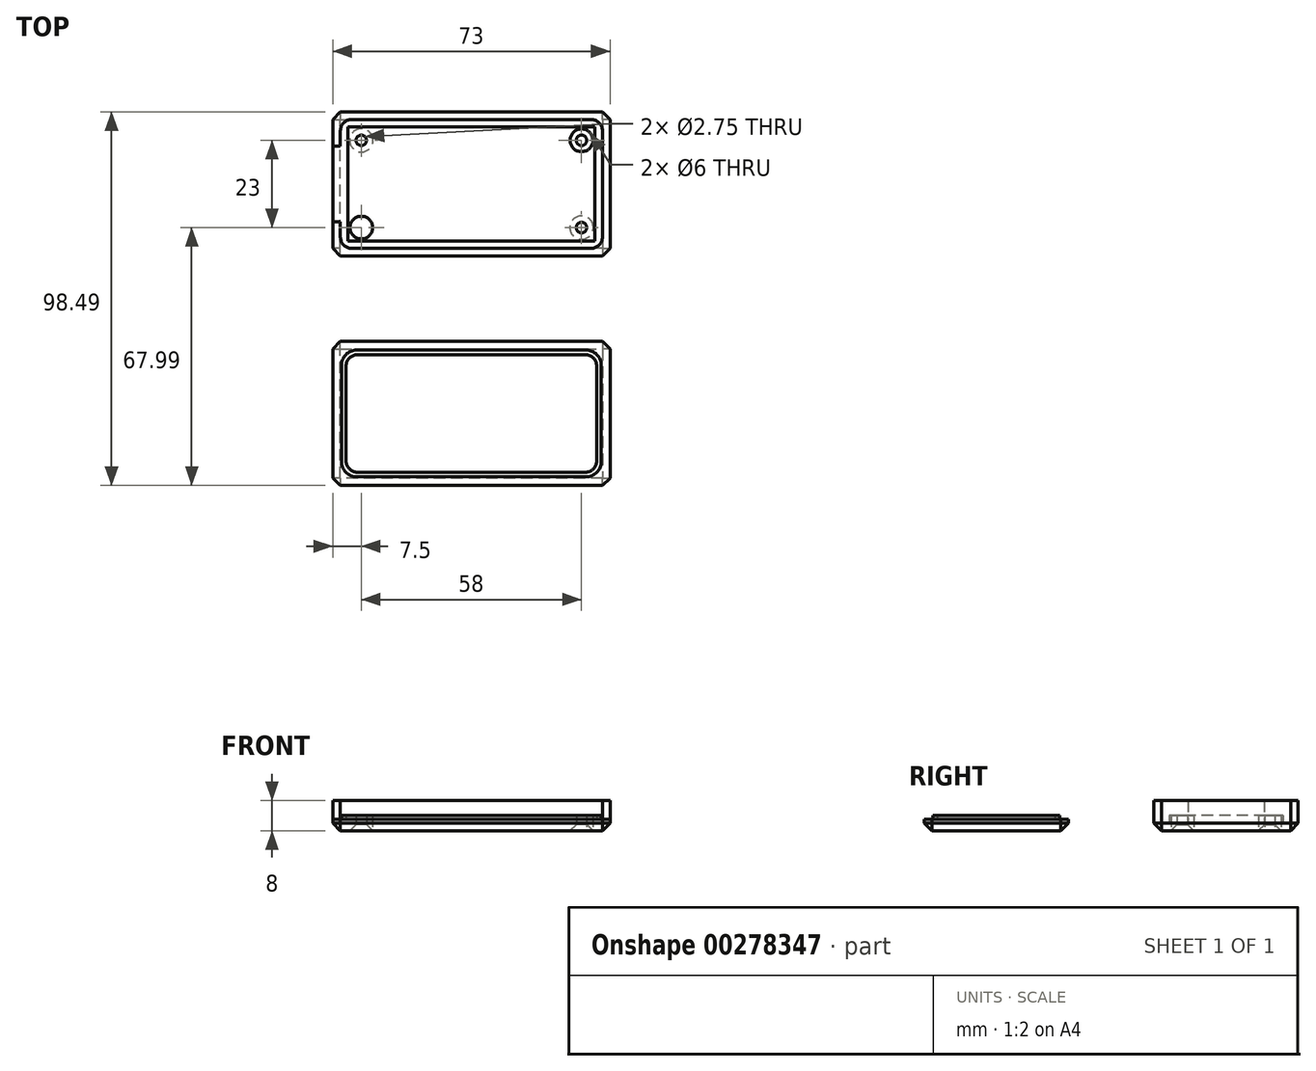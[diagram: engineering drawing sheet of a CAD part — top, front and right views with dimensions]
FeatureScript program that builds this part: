
annotation { "Feature Type Name" : "Feature", "Feature Type Description" : "" }
export const myFeature = defineFeature(function(context is Context, id is Id, definition is map)
    precondition{}
    {
        {
            var Q0;
            Q0=qCreatedBy(makeId("Top.planeOp"),FACE);
            var sketch = newSketch(context, id + "F0", { "sketchPlane" : qUnion([Q0])});
            skLineSegment(sketch, "E0.bottom", {"start": v(-32.5, 15) * mm, "end": v(32.5, 15) * mm});
            skLineSegment(sketch, "E0.top", {"start": v(-32.5, -15) * mm, "end": v(32.5, -15) * mm});
            skLineSegment(sketch, "E0.left", {"start": v(-32.5, 15) * mm, "end": v(-32.5, -15) * mm});
            skLineSegment(sketch, "E0.right", {"start": v(32.5, 15) * mm, "end": v(32.5, -15) * mm});
            skPoint(sketch, "E0.middle", {"position": v(0, 0) * mm});
            skLineSegment(sketch, "E1", {"start": v(-32.5, 15) * mm, "end": v(-32.5, 11.5) * mm, "construction": true});
            skLineSegment(sketch, "E2", {"start": v(-32.5, 11.5) * mm, "end": v(-29, 11.5) * mm, "construction": true});
            skCircle(sketch, "E3", {"center": v(-29, 11.5) * mm, "radius": 1.38 * mm});
            skCircle(sketch, "E4", {"center": v(-29, 11.5) * mm, "radius": 3 * mm});
            skCircle(sketch, "E5.MirrorC", {"center": v(29, 11.5) * mm, "radius": 1.38 * mm});
            skCircle(sketch, "E6.MirrorC", {"center": v(29, 11.5) * mm, "radius": 3 * mm});
            skCircle(sketch, "E7.MirrorC", {"center": v(29, -11.5) * mm, "radius": 1.38 * mm});
            skCircle(sketch, "E8.MirrorC", {"center": v(29, -11.5) * mm, "radius": 3 * mm});
            skCircle(sketch, "E9.MirrorC", {"center": v(-29, -11.5) * mm, "radius": 3 * mm});
            skCircle(sketch, "E10.MirrorC", {"center": v(-29, -11.5) * mm, "radius": 1.38 * mm});
            skLineSegment(sketch, "E11.0", {"start": v(-34.5, 17) * mm, "end": v(34.5, 17) * mm});
            skLineSegment(sketch, "E11.1", {"start": v(-34.5, 17) * mm, "end": v(-34.5, -17) * mm});
            skLineSegment(sketch, "E11.2", {"start": v(-34.5, -17) * mm, "end": v(34.5, -17) * mm});
            skLineSegment(sketch, "E11.3", {"start": v(34.5, 17) * mm, "end": v(34.5, -17) * mm});
            skLineSegment(sketch, "E12.0", {"start": v(-36.5, 19) * mm, "end": v(36.5, 19) * mm});
            skLineSegment(sketch, "E12.1", {"start": v(-36.5, 19) * mm, "end": v(-36.5, -19) * mm});
            skLineSegment(sketch, "E12.2", {"start": v(-36.5, -19) * mm, "end": v(36.5, -19) * mm});
            skLineSegment(sketch, "E12.3", {"start": v(36.5, 19) * mm, "end": v(36.5, -19) * mm});
            skLineSegment(sketch, "E13", {"start": v(-36.5, 0) * mm, "end": v(-36.5, 10) * mm, "construction": true});
            skLineSegment(sketch, "E14", {"start": v(-36.5, 10) * mm, "end": v(-34.5, 10) * mm});
            skLineSegment(sketch, "E15.MirrorCS", {"start": v(-36.5, -10) * mm, "end": v(-34.5, -10) * mm});
            skSolve(sketch);
        }
        {
            var Q0;
            Q0=makeQuery(id+"F0.imprint","IMPRINT",FACE,{"disambiguationData":[TD([[makeQuery(id+"F0.imprint","IMPRINT",EDGE,{"derivedFrom":sQuery(id+"F0.wireOp",EDGE,"E11.0")}),1.0]])]});
            var Q1;
            Q1=makeQuery(id+"F0.imprint","IMPRINT",FACE,{"disambiguationData":[TD([[makeQuery(id+"F0.imprint","IMPRINT",EDGE,{"derivedFrom":sQuery(id+"F0.wireOp",EDGE,"E0.bottom")}),1.0]])]});
            var Q2;
            Q2=makeQuery(id+"F0.imprint","IMPRINT",FACE,{"disambiguationData":[TD([[makeQuery(id+"F0.imprint","IMPRINT",EDGE,{"derivedFrom":sQuery(id+"F0.wireOp",EDGE,"E0.bottom")}),-1.0]])]});
            var Q3;
            Q3=makeQuery(id+"F0.imprint","IMPRINT",FACE,{"disambiguationData":[TD([[makeQuery(id+"F0.imprint","IMPRINT",EDGE,{"derivedFrom":sQuery(id+"F0.wireOp",EDGE,"E3")}),-1.0]])]});
            var Q4;
            Q4=makeQuery(id+"F0.imprint","IMPRINT",FACE,{"disambiguationData":[TD([[makeQuery(id+"F0.imprint","IMPRINT",EDGE,{"derivedFrom":sQuery(id+"F0.wireOp",EDGE,"E5.MirrorC")}),1.0]])]});
            var Q5;
            Q5=makeQuery(id+"F0.imprint","IMPRINT",FACE,{"disambiguationData":[TD([[makeQuery(id+"F0.imprint","IMPRINT",EDGE,{"derivedFrom":sQuery(id+"F0.wireOp",EDGE,"E7.MirrorC")}),-1.0]])]});
            var Q6;
            Q6=makeQuery(id+"F0.imprint","IMPRINT",FACE,{"disambiguationData":[TD([[makeQuery(id+"F0.imprint","IMPRINT",EDGE,{"derivedFrom":sQuery(id+"F0.wireOp",EDGE,"E9.MirrorC")}),-1.0]])]});
            var Q7;
            {var subQ0=sQuery(id+"F0.wireOp",EDGE,"E14");Q7=makeQuery(id+"F0.imprint","IMPRINT",FACE,{"disambiguationData":[TD([[makeQuery(id+"F0.imprint","IMPRINT",EDGE,{"derivedFrom":subQ0}),-1.0]])]});}
            extrude(context, id + "F1", {"entities" : qUnion([Q0, Q1, Q2, Q3, Q4, Q5, Q6, Q7]), "depth" : 2 * mm});
        }
        {
            var Q0;
            Q0=makeQuery(id+"F0.imprint","IMPRINT",FACE,{"disambiguationData":[TD([[makeQuery(id+"F0.imprint","IMPRINT",EDGE,{"derivedFrom":sQuery(id+"F0.wireOp",EDGE,"E9.MirrorC")}),-1.0]])]});
            var Q1;
            Q1=makeQuery(id+"F0.imprint","IMPRINT",FACE,{"disambiguationData":[TD([[makeQuery(id+"F0.imprint","IMPRINT",EDGE,{"derivedFrom":sQuery(id+"F0.wireOp",EDGE,"E3")}),-1.0]])]});
            var Q2;
            Q2=makeQuery(id+"F0.imprint","IMPRINT",FACE,{"disambiguationData":[TD([[makeQuery(id+"F0.imprint","IMPRINT",EDGE,{"derivedFrom":sQuery(id+"F0.wireOp",EDGE,"E7.MirrorC")}),-1.0]])]});
            var Q3;
            Q3=makeQuery(id+"F0.imprint","IMPRINT",FACE,{"disambiguationData":[TD([[makeQuery(id+"F0.imprint","IMPRINT",EDGE,{"derivedFrom":sQuery(id+"F0.wireOp",EDGE,"E5.MirrorC")}),1.0]])]});
            extrude(context, id + "F2", {"entities" : qUnion([Q0, Q1, Q2, Q3]), "operationType" : NewBodyOperationType.ADD, "depth" : 4 * mm});
        }
        {
            var Q0;
            Q0=makeQuery(id+"F0.imprint","IMPRINT",FACE,{"disambiguationData":[TD([[makeQuery(id+"F0.imprint","IMPRINT",EDGE,{"derivedFrom":sQuery(id+"F0.wireOp",EDGE,"E11.0")}),1.0]])]});
            extrude(context, id + "F3", {"entities" : qUnion([Q0]), "operationType" : NewBodyOperationType.ADD, "depth" : 8 * mm});
        }
        {
            var Q0;
            Q0=makeQuery(id+"F3.opExtrude","SWEPT_EDGE",EDGE,{"disambiguationData":[OSD([sQuery(id+"F0.wireOp",EDGE,"E11.0"),sQuery(id+"F0.wireOp",EDGE,"E11.1")])]});
            var Q1;
            Q1=makeQuery(id+"F3.opExtrude","SWEPT_EDGE",EDGE,{"disambiguationData":[OSD([sQuery(id+"F0.wireOp",EDGE,"E11.1"),sQuery(id+"F0.wireOp",EDGE,"E11.2")])]});
            var Q2;
            Q2=makeQuery(id+"F3.opExtrude","SWEPT_EDGE",EDGE,{"disambiguationData":[OSD([sQuery(id+"F0.wireOp",EDGE,"E11.2"),sQuery(id+"F0.wireOp",EDGE,"E11.3")])]});
            var Q3;
            Q3=makeQuery(id+"F3.opExtrude","SWEPT_EDGE",EDGE,{"disambiguationData":[OSD([sQuery(id+"F0.wireOp",EDGE,"E11.0"),sQuery(id+"F0.wireOp",EDGE,"E11.3")])]});
            fillet(context, id + "F4", {"entities" : qUnion([Q0, Q1, Q2, Q3]), "radius" : 3 * mm, "tangentPropagation" : true, "allowEdgeOverflow" : false});
        }
        {
            var Q0;
            {var subQ0=sQuery(id+"F0.wireOp",EDGE,"E12.3");var subQ1=sQuery(id+"F0.wireOp",EDGE,"E12.2");Q0=makeQuery(id+"F3.boolean.opBoolean","MERGE",EDGE,{"derivedFrom":[makeQuery(id+"F1.opExtrude","SWEPT_EDGE",EDGE,{"disambiguationData":[OSD([subQ1,subQ0])]}),makeQuery(id+"F3.opExtrude","SWEPT_EDGE",EDGE,{"disambiguationData":[OSD([subQ1,subQ0])]})]});}
            var Q1;
            {var subQ0=sQuery(id+"F0.wireOp",EDGE,"E12.3");var subQ1=sQuery(id+"F0.wireOp",EDGE,"E12.0");Q1=makeQuery(id+"F3.boolean.opBoolean","MERGE",EDGE,{"derivedFrom":[makeQuery(id+"F1.opExtrude","SWEPT_EDGE",EDGE,{"disambiguationData":[OSD([subQ1,subQ0])]}),makeQuery(id+"F3.opExtrude","SWEPT_EDGE",EDGE,{"disambiguationData":[OSD([subQ1,subQ0])]})]});}
            var Q2;
            {var subQ0=sQuery(id+"F0.wireOp",EDGE,"E12.1");var subQ1=sQuery(id+"F0.wireOp",EDGE,"E12.0");Q2=makeQuery(id+"F3.boolean.opBoolean","MERGE",EDGE,{"derivedFrom":[makeQuery(id+"F1.opExtrude","SWEPT_EDGE",EDGE,{"disambiguationData":[OSD([subQ1,subQ0])]}),makeQuery(id+"F3.opExtrude","SWEPT_EDGE",EDGE,{"disambiguationData":[OSD([subQ1,subQ0])]})]});}
            var Q3;
            {var subQ0=sQuery(id+"F0.wireOp",EDGE,"E12.2");var subQ1=sQuery(id+"F0.wireOp",EDGE,"E12.1");Q3=makeQuery(id+"F3.boolean.opBoolean","MERGE",EDGE,{"derivedFrom":[makeQuery(id+"F1.opExtrude","SWEPT_EDGE",EDGE,{"disambiguationData":[OSD([subQ1,subQ0])]}),makeQuery(id+"F3.opExtrude","SWEPT_EDGE",EDGE,{"disambiguationData":[OSD([subQ1,subQ0])]})]});}
            var Q4;
            Q4=makeQuery(id+"F1.opExtrude","CAP_EDGE",EDGE,{"disambiguationData":[OSD([sQuery(id+"F0.wireOp",EDGE,"E12.2")])],"isStart":true});
            var Q5;
            Q5=makeQuery(id+"F1.opExtrude","CAP_EDGE",EDGE,{"disambiguationData":[OSD([sQuery(id+"F0.wireOp",EDGE,"E12.1")])],"isStart":true});
            var Q6;
            Q6=makeQuery(id+"F1.opExtrude","CAP_EDGE",EDGE,{"disambiguationData":[OSD([sQuery(id+"F0.wireOp",EDGE,"E12.0")])],"isStart":true});
            var Q7;
            Q7=makeQuery(id+"F1.opExtrude","CAP_EDGE",EDGE,{"disambiguationData":[OSD([sQuery(id+"F0.wireOp",EDGE,"E12.3")])],"isStart":true});
            chamfer(context, id + "F5", {"entities" : qUnion([Q0, Q1, Q2, Q3, Q4, Q5, Q6, Q7]), "width" : 2 * mm, "tangentPropagation" : true});
        }
        {
            var Q0;
            Q0=makeQuery(id+"F1.opExtrude","CAP_EDGE",EDGE,{"disambiguationData":[OSD([sQuery(id+"F0.wireOp",EDGE,"E5.MirrorC")])],"isStart":true});
            var Q1;
            Q1=makeQuery(id+"F1.opExtrude","CAP_EDGE",EDGE,{"disambiguationData":[OSD([sQuery(id+"F0.wireOp",EDGE,"E7.MirrorC")])],"isStart":true});
            var Q2;
            Q2=makeQuery(id+"F1.opExtrude","CAP_EDGE",EDGE,{"disambiguationData":[OSD([sQuery(id+"F0.wireOp",EDGE,"E10.MirrorC")])],"isStart":true});
            var Q3;
            Q3=makeQuery(id+"F1.opExtrude","CAP_EDGE",EDGE,{"disambiguationData":[OSD([sQuery(id+"F0.wireOp",EDGE,"E3")])],"isStart":true});
            chamfer(context, id + "F6", {"entities" : qUnion([Q0, Q1, Q2, Q3]), "width" : 1.7 * mm, "tangentPropagation" : true});
        }
        {
            var Q0;
            Q0=qCreatedBy(makeId("Top.planeOp"),FACE);
            var sketch = newSketch(context, id + "F7", { "sketchPlane" : qUnion([Q0])});
            skLineSegment(sketch, "E16.bottom", {"start": v(32.5, -45.5) * mm, "end": v(-32.5, -45.5) * mm});
            skLineSegment(sketch, "E16.top", {"start": v(32.5, -75.5) * mm, "end": v(-32.5, -75.5) * mm});
            skLineSegment(sketch, "E16.left", {"start": v(32.5, -45.5) * mm, "end": v(32.5, -75.5) * mm});
            skLineSegment(sketch, "E16.right", {"start": v(-32.5, -45.5) * mm, "end": v(-32.5, -75.5) * mm});
            skPoint(sketch, "E16.middle", {"position": v(0, -60.5) * mm});
            skLineSegment(sketch, "E17.0", {"start": v(34.2, -43.8) * mm, "end": v(-34.2, -43.8) * mm});
            skLineSegment(sketch, "E17.1", {"start": v(34.2, -43.8) * mm, "end": v(34.2, -77.2) * mm});
            skLineSegment(sketch, "E17.2", {"start": v(34.2, -77.2) * mm, "end": v(-34.2, -77.2) * mm});
            skLineSegment(sketch, "E17.3", {"start": v(-34.2, -43.8) * mm, "end": v(-34.2, -77.2) * mm});
            skLineSegment(sketch, "E18.0", {"start": v(36.5, -41.5) * mm, "end": v(-36.5, -41.5) * mm});
            skLineSegment(sketch, "E18.1", {"start": v(36.5, -41.5) * mm, "end": v(36.5, -79.5) * mm});
            skLineSegment(sketch, "E18.2", {"start": v(36.5, -79.5) * mm, "end": v(-36.5, -79.5) * mm});
            skLineSegment(sketch, "E18.3", {"start": v(-36.5, -41.5) * mm, "end": v(-36.5, -79.5) * mm});
            skLineSegment(sketch, "E19.0", {"start": v(33, -45) * mm, "end": v(-33, -45) * mm});
            skLineSegment(sketch, "E19.1", {"start": v(33, -45) * mm, "end": v(33, -76) * mm});
            skLineSegment(sketch, "E19.2", {"start": v(33, -76) * mm, "end": v(-33, -76) * mm});
            skLineSegment(sketch, "E19.3", {"start": v(-33, -45) * mm, "end": v(-33, -76) * mm});
            skSolve(sketch);
        }
        {
            var Q0;
            Q0=makeQuery(id+"F7.imprint","IMPRINT",FACE,{"disambiguationData":[TD([[makeQuery(id+"F7.imprint","IMPRINT",EDGE,{"derivedFrom":sQuery(id+"F7.wireOp",EDGE,"E17.0")}),-1.0]])]});
            var Q1;
            Q1=makeQuery(id+"F7.imprint","IMPRINT",FACE,{"disambiguationData":[TD([[makeQuery(id+"F7.imprint","IMPRINT",EDGE,{"derivedFrom":sQuery(id+"F7.wireOp",EDGE,"E17.0")}),1.0]])]});
            var Q2;
            Q2=makeQuery(id+"F7.imprint","IMPRINT",FACE,{"disambiguationData":[TD([[makeQuery(id+"F7.imprint","IMPRINT",EDGE,{"derivedFrom":sQuery(id+"F7.wireOp",EDGE,"E16.bottom")}),-1.0]])]});
            var Q3;
            Q3=makeQuery(id+"F7.imprint","IMPRINT",FACE,{"disambiguationData":[TD([[makeQuery(id+"F7.imprint","IMPRINT",EDGE,{"derivedFrom":sQuery(id+"F7.wireOp",EDGE,"E16.bottom")}),1.0]])]});
            extrude(context, id + "F8", {"entities" : qUnion([Q0, Q1, Q2, Q3]), "depth" : 3 * mm});
        }
        {
            var Q0;
            Q0=makeQuery(id+"F7.imprint","IMPRINT",FACE,{"disambiguationData":[TD([[makeQuery(id+"F7.imprint","IMPRINT",EDGE,{"derivedFrom":sQuery(id+"F7.wireOp",EDGE,"E17.0")}),1.0]])]});
            extrude(context, id + "F9", {"entities" : qUnion([Q0]), "operationType" : NewBodyOperationType.ADD, "depth" : 4 * mm});
        }
        {
            var Q0;
            Q0=makeQuery(id+"F9.opExtrude","SWEPT_EDGE",EDGE,{"disambiguationData":[OSD([sQuery(id+"F7.wireOp",EDGE,"E19.0"),sQuery(id+"F7.wireOp",EDGE,"E19.1")])]});
            var Q1;
            Q1=makeQuery(id+"F9.opExtrude","SWEPT_EDGE",EDGE,{"disambiguationData":[OSD([sQuery(id+"F7.wireOp",EDGE,"E19.0"),sQuery(id+"F7.wireOp",EDGE,"E19.3")])]});
            var Q2;
            Q2=makeQuery(id+"F9.opExtrude","SWEPT_EDGE",EDGE,{"disambiguationData":[OSD([sQuery(id+"F7.wireOp",EDGE,"E19.2"),sQuery(id+"F7.wireOp",EDGE,"E19.3")])]});
            var Q3;
            Q3=makeQuery(id+"F9.opExtrude","SWEPT_EDGE",EDGE,{"disambiguationData":[OSD([sQuery(id+"F7.wireOp",EDGE,"E19.1"),sQuery(id+"F7.wireOp",EDGE,"E19.2")])]});
            fillet(context, id + "F10", {"entities" : qUnion([Q0, Q1, Q2, Q3]), "radius" : 3 * mm, "tangentPropagation" : true, "allowEdgeOverflow" : false});
        }
        {
            var Q0;
            Q0=makeQuery(id+"F9.opExtrude","SWEPT_EDGE",EDGE,{"disambiguationData":[OSD([sQuery(id+"F7.wireOp",EDGE,"E17.0"),sQuery(id+"F7.wireOp",EDGE,"E17.3")])]});
            var Q1;
            Q1=makeQuery(id+"F9.opExtrude","SWEPT_EDGE",EDGE,{"disambiguationData":[OSD([sQuery(id+"F7.wireOp",EDGE,"E17.2"),sQuery(id+"F7.wireOp",EDGE,"E17.3")])]});
            var Q2;
            Q2=makeQuery(id+"F9.opExtrude","SWEPT_EDGE",EDGE,{"disambiguationData":[OSD([sQuery(id+"F7.wireOp",EDGE,"E17.1"),sQuery(id+"F7.wireOp",EDGE,"E17.2")])]});
            var Q3;
            Q3=makeQuery(id+"F9.opExtrude","SWEPT_EDGE",EDGE,{"disambiguationData":[OSD([sQuery(id+"F7.wireOp",EDGE,"E17.0"),sQuery(id+"F7.wireOp",EDGE,"E17.1")])]});
            fillet(context, id + "F11", {"entities" : qUnion([Q0, Q1, Q2, Q3]), "radius" : 4 * mm, "tangentPropagation" : true, "allowEdgeOverflow" : false});
        }
        {
            var Q0;
            Q0=makeQuery(id+"F8.opExtrude","SWEPT_EDGE",EDGE,{"disambiguationData":[OSD([sQuery(id+"F7.wireOp",EDGE,"E18.1"),sQuery(id+"F7.wireOp",EDGE,"E18.2")])]});
            var Q1;
            Q1=makeQuery(id+"F8.opExtrude","SWEPT_EDGE",EDGE,{"disambiguationData":[OSD([sQuery(id+"F7.wireOp",EDGE,"E18.0"),sQuery(id+"F7.wireOp",EDGE,"E18.1")])]});
            var Q2;
            Q2=makeQuery(id+"F8.opExtrude","SWEPT_EDGE",EDGE,{"disambiguationData":[OSD([sQuery(id+"F7.wireOp",EDGE,"E18.0"),sQuery(id+"F7.wireOp",EDGE,"E18.3")])]});
            var Q3;
            Q3=makeQuery(id+"F8.opExtrude","SWEPT_EDGE",EDGE,{"disambiguationData":[OSD([sQuery(id+"F7.wireOp",EDGE,"E18.2"),sQuery(id+"F7.wireOp",EDGE,"E18.3")])]});
            var Q4;
            Q4=makeQuery(id+"F8.opExtrude","CAP_EDGE",EDGE,{"disambiguationData":[OSD([sQuery(id+"F7.wireOp",EDGE,"E18.3")])],"isStart":true});
            var Q5;
            Q5=makeQuery(id+"F8.opExtrude","CAP_EDGE",EDGE,{"disambiguationData":[OSD([sQuery(id+"F7.wireOp",EDGE,"E18.1")])],"isStart":true});
            var Q6;
            Q6=makeQuery(id+"F8.opExtrude","CAP_EDGE",EDGE,{"disambiguationData":[OSD([sQuery(id+"F7.wireOp",EDGE,"E18.0")])],"isStart":true});
            var Q7;
            Q7=makeQuery(id+"F8.opExtrude","CAP_EDGE",EDGE,{"disambiguationData":[OSD([sQuery(id+"F7.wireOp",EDGE,"E18.2")])],"isStart":true});
            chamfer(context, id + "F12", {"entities" : qUnion([Q0, Q1, Q2, Q3, Q4, Q5, Q6, Q7]), "width" : 2 * mm, "tangentPropagation" : true});
        }
    });
